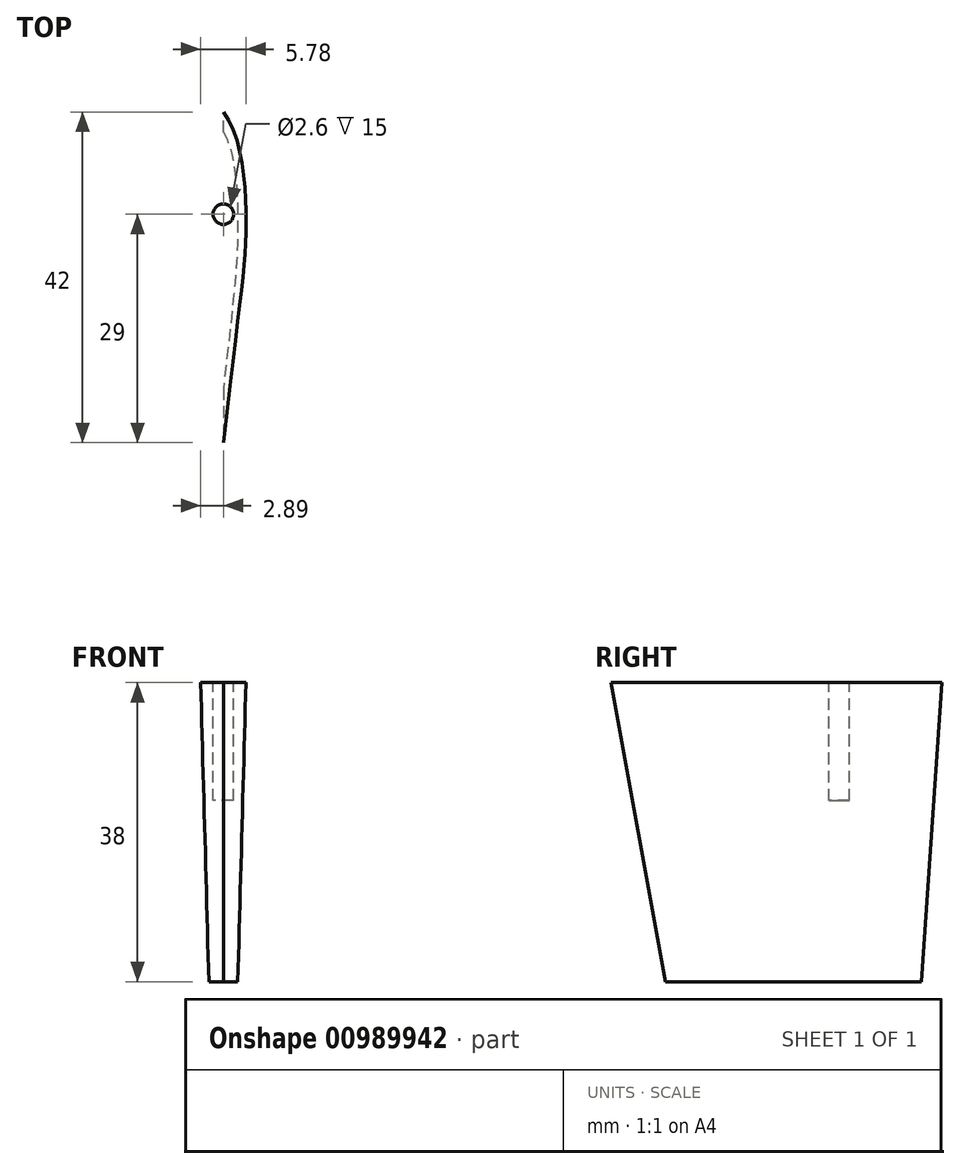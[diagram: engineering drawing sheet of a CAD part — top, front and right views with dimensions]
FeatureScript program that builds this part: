
annotation { "Feature Type Name" : "Feature", "Feature Type Description" : "" }
export const myFeature = defineFeature(function(context is Context, id is Id, definition is map)
    precondition{}
    {
        {
            var Q0;
            Q0=qCreatedBy(makeId("Top.planeOp"),FACE);
            var sketch = newSketch(context, id + "F0", { "sketchPlane" : qUnion([Q0])});
            skLineSegment(sketch, "E0", {"start": v(0, 0) * mm, "end": v(0, 13) * mm});
            skLineSegment(sketch, "E1", {"start": v(0, 0) * mm, "end": v(0, -29) * mm});
            skFitSpline(sketch, "E2", {"points": [v(0, 13) * mm, v(-2.88, 0) * mm, v(0, -29) * mm], "startDerivative": vector(-17.15, -22.3) * mm, "endDerivative": vector(10.73, -93.76) * mm});
            skFitSpline(sketch, "E3.MirrorCS", {"points": [v(0, 13) * mm, v(2.88, 0) * mm, v(0, -29) * mm], "startDerivative": vector(17.15, -22.3) * mm, "endDerivative": vector(-10.73, -93.76) * mm});
            skSolve(sketch);
        }
        {
            var Q0;
            Q0=qCreatedBy(makeId("Top.planeOp"),FACE);
            cPlane(context, id + "F1", {"entities" : qUnion([Q0]), "cplaneType" : CPlaneType.OFFSET, "offset" : 38 * mm, "oppositeDirection" : true, "width" : 150 * mm, "height" : 150 * mm});
        }
        {
            var Q0;
            Q0=qCreatedBy(id+"F1.planeOp",FACE);
            var sketch = newSketch(context, id + "F2", { "sketchPlane" : qUnion([Q0])});
            skLineSegment(sketch, "E4", {"start": v(0, 10.4) * mm, "end": v(0, 0) * mm});
            skLineSegment(sketch, "E5", {"start": v(0, 0) * mm, "end": v(0, -22.09) * mm});
            skFitSpline(sketch, "E6", {"points": [v(0, 10.4) * mm, v(1.82, 0) * mm, v(0, -22.09) * mm], "startDerivative": vector(11.35, -18.52) * mm, "endDerivative": vector(-8.67, -73.02) * mm});
            skFitSpline(sketch, "E7.MirrorCS", {"points": [v(0, 10.4) * mm, v(-1.82, 0) * mm, v(0, -22.09) * mm], "startDerivative": vector(-11.35, -18.52) * mm, "endDerivative": vector(8.67, -73.02) * mm});
            skSolve(sketch);
        }
        {
            var Q0;
            Q0 = qSketchRegion(id + "F2", true);
            var Q1;
            Q1 = qSketchRegion(id + "F0", true);
            loft(context, id + "F3", {"sheetProfilesArray" : [{ "sheetProfileEntities" : qUnion([Q0]) }, { "sheetProfileEntities" : qUnion([Q1]) }]});
        }
        {
            var Q0;
            Q0=qCreatedBy(makeId("Top.planeOp"),FACE);
            var sketch = newSketch(context, id + "F4", { "sketchPlane" : qUnion([Q0])});
            skCircle(sketch, "E8", {"center": v(0, 0) * mm, "radius": 1.3 * mm});
            skSolve(sketch);
        }
        {
            var Q0;
            Q0 = qSketchRegion(id + "F4", true);
            extrude(context, id + "F5", {"entities" : qUnion([Q0]), "operationType" : NewBodyOperationType.REMOVE, "oppositeDirection" : true, "depth" : 15 * mm, "offsetDistance" : 25 * mm});
        }
    });
